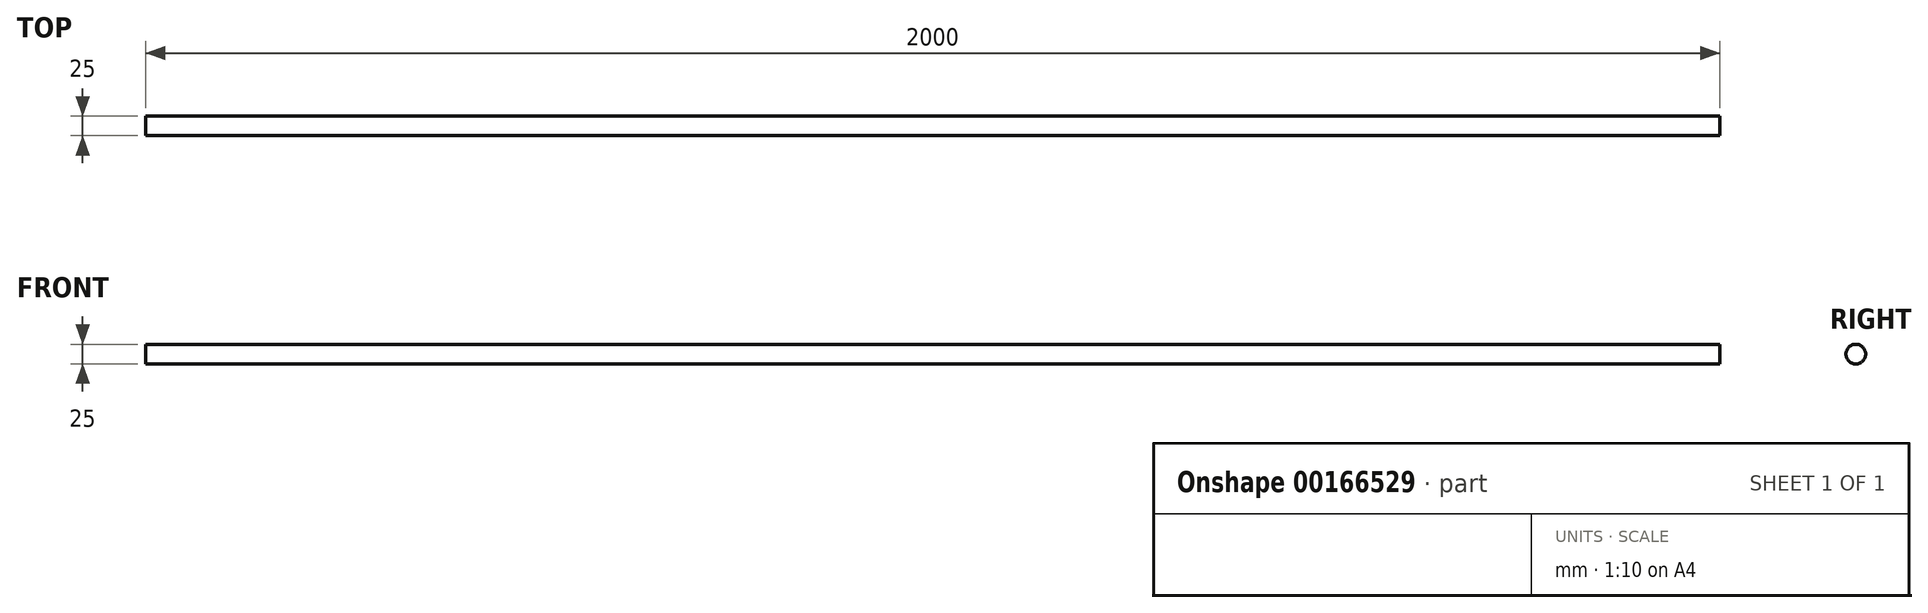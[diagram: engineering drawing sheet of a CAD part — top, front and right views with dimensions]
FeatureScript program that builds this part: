
annotation { "Feature Type Name" : "Feature", "Feature Type Description" : "" }
export const myFeature = defineFeature(function(context is Context, id is Id, definition is map)
    precondition{}
    {
        {
            var Q0;
            Q0=qCreatedBy(makeId("Right.planeOp"),FACE);
            var sketch = newSketch(context, id + "F0", { "sketchPlane" : qUnion([Q0])});
            skCircle(sketch, "E0", {"center": v(0, 0) * mm, "radius": 12.5 * mm});
            skSolve(sketch);
        }
        {
            var Q0;
            Q0=makeQuery(id+"F0.imprint","IMPRINT",FACE,{"disambiguationData":[TD([[makeQuery(id+"F0.imprint","IMPRINT",EDGE,{"derivedFrom":sQuery(id+"F0.wireOp",EDGE,"E0")}),1.0]])]});
            extrude(context, id + "F1", {"entities" : qUnion([Q0]), "depth" : 2000 * mm});
        }
    });
